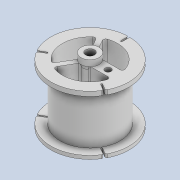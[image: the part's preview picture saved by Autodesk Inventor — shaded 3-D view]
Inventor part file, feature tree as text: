
AUTODESK INVENTOR PART (.ipt)
format: ipt  version: 2020 (Build 240168000, 168)  size: 469,504 bytes
history: native  units: mm
features: extrude x9, thicken_offset x9, sketch x9, projected_geometry x5, fillet x4, pattern_circular x1
ambient origin geometry x8: Origin, YZ Plane, XZ Plane, XY Plane, X Axis, Y Axis, Z Axis, Center Point
bodies: Solid1 (feature_tree)
feature tree (37):
  extrude  "Extrusion1"  Depth=20.0mm TaperAngle=0.0deg
  extrude  "Extrusion2"  Depth=2.0mm TaperAngle=0.0deg
  extrude  "Extrusion3"  Depth=2.0mm
  extrude  "Extrusion4"  Depth=6.0mm
  extrude  "Extrusion5"  Depth=2.0mm TaperAngle=0.0deg
  extrude  "Extrusion6"  Depth=2.0mm TaperAngle=0.0deg
  extrude  "Extrusion7"  Depth=2.0mm
  fillet  "Fillet1"  Radius=2.0mm
  pattern_circular  "Circular Pattern1"  Count=3 Angle=360.0deg
  extrude  "Extrusion8"  Depth=2.0mm
  fillet  "Fillet2"  Radius=4.0mm
  extrude  "Extrusion9"  Depth=2.0mm
  fillet  "Fillet3"  [1 undecoded]
  thicken_offset  "Thicken1"
  thicken_offset  "Thicken2"
  thicken_offset  "Thicken3"
  thicken_offset  "Thicken4"
  thicken_offset  "Thicken5"
  thicken_offset  "Thicken6"
  thicken_offset  "Thicken7"
  thicken_offset  "Thicken8"
  thicken_offset  "Thicken9"
  fillet  "Fillet5"  [1 undecoded]
  sketch  "Sketch1"  dims[d0=20.0mm d1=20.0mm d2=0.0mm]
  sketch  "Sketch2"  dims[d3=3.0mm d4=2.0mm d5=0.0mm]
  sketch  "Sketch3"  dims[d6=2.0mm d7=0.0mm d8=3.0mm]
  projected_geometry  "Projected Loop1"
  sketch  "Sketch4"  dims[d9=20.0mm d10=0.0mm d11=6.0mm]
  sketch  "Sketch5"  dims[d12=2.0mm d13=20.0mm d14=0.0mm]
  projected_geometry  "Projected Loop2"
  sketch  "Sketch6"  dims[d15=1.5mm d16=2.0mm d17=0.0mm]
  sketch  "Sketch7"  dims[d18=0.5mm d19=5.5mm d20=2.0mm d21=0.0mm]
  projected_geometry  "Projected Loop3"
  sketch  "Sketch8"  dims[d22=0.25mm d23=30.0mm d24=360.0deg]
  projected_geometry  "Projected Loop4"
  sketch  "Sketch9"  dims[d26=1.5mm d27=0.7mm d28=4.0mm d29=6.0mm d30=60.0deg d31=60.0deg d32=1.6mm d33=10.0mm d34=1.6mm d35=10.0mm d36=20.0mm d37=0.0mm d38=0.8mm d39=20.0mm d40=0.0mm d41=0.5mm d43=0.5mm d44=0.5mm d45=0.5mm d46=0.5mm d47=0.35mm d48=0.35mm d49=0.7mm d50=0.7mm d51=0.7mm d52=0.7mm d53=0.7mm d54=0.7mm d55=1.0mm d56=1.0mm d57=1.0mm d58=1.0mm d59=1.0mm d60=1.0mm d66=2.0mm]
  projected_geometry  "Projected Loop5"
note: 2 required parameter values undecoded (feature->parameter linkage not recoverable at this tier; creation-order binding heuristic only, values carry confidence <= 0.55)
